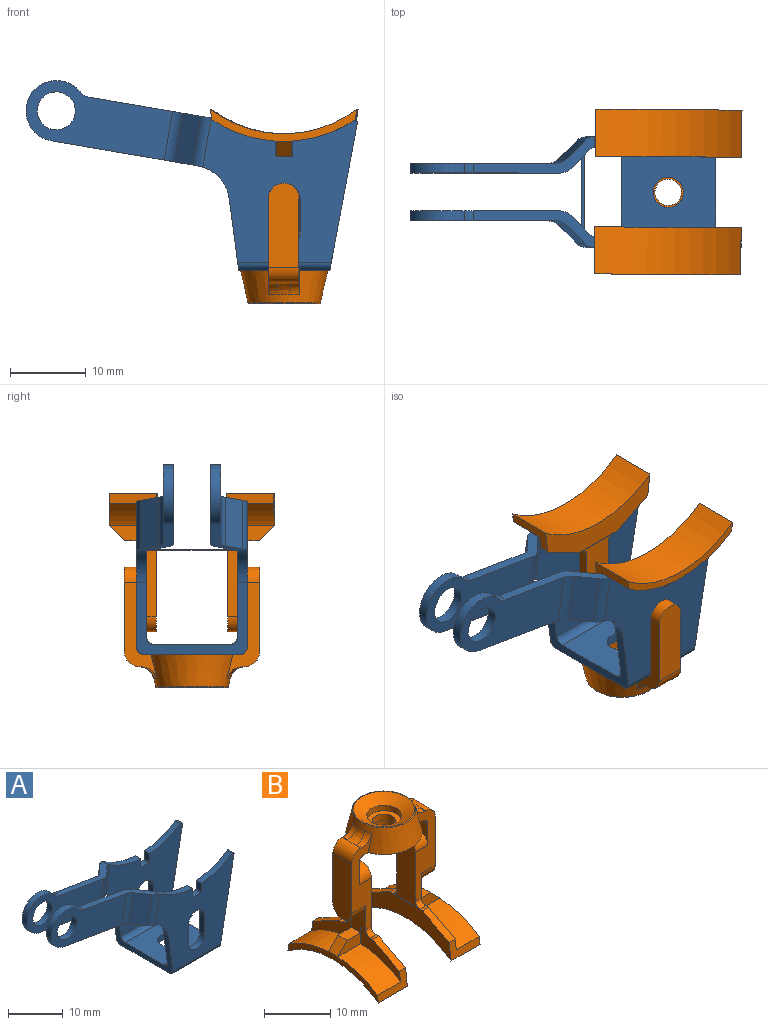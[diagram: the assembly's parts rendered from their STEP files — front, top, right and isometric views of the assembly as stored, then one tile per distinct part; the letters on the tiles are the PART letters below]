
ASSEMBLY  parts=2 mates=1
PART A: 66 faces, bbox 43.6x14.6x25 mm
  f0: plane 19.31x4.69mm, normal (-0.17,0,-0.99), area 27.2mm2, adj f4,f14,f45,f48,f49,f50,f54,f55
  f1: plane 19.31x4.69mm, normal (-0.17,0,-0.99), area 27.2mm2, adj f5,f14,f42,f43,f46,f47,f53,f57
  f2: cylinder r=2mm len=1.3mm, axis (0,1,0), area 1.9mm2, adj f4,f6,f45,f49
  f3: cylinder r=2mm len=1.3mm, axis (0,1,0), area 1.9mm2, adj f5,f7,f42,f46
  f4: cylinder r=4mm len=7.94mm, axis (0,1,0), area 20.1mm2, adj f0,f2,f45,f49
  f5: cylinder r=4mm len=7.94mm, axis (0,1,0), area 20.1mm2, adj f1,f3,f42,f46
  f6: plane 15.92x4.8mm, normal (0.17,0,0.99), area 22.9mm2, adj f2,f11,f45,f48,f49,f50,f54,f55
  f7: plane 15.92x4.8mm, normal (0.17,0,0.99), area 22.9mm2, adj f3,f10,f42,f43,f46,f47,f53,f57
  f8: plane 20.35x18.99mm, normal (0,-1,0), area 231.1mm2, adj f11,f14,f15,f17,f18,f19,f33,f34
  f9: plane 20.35x18.99mm, normal (0,1,0), area 231.1mm2, adj f10,f12,f13,f14,f15,f17,f24,f25
  f10: cylinder r=17mm len=8.63mm, axis (0,1,0), area 12.1mm2, adj f7,f9,f22,f31,f57,f59
  f11: cylinder r=17mm len=8.63mm, axis (0,1,0), area 12.1mm2, adj f6,f8,f21,f41,f56,f60
  f12: cylinder r=0.3mm len=1.3mm, axis (0,1,0), area 0.9mm2, adj f9,f13,f17,f22
  f13: cylinder r=17mm len=8.04mm, axis (0,1,0), area 11.1mm2, adj f9,f12,f22,f28
  f14: cylinder r=5mm len=14.6mm, axis (0,1,0), area 21mm2, adj f0,f1,f8,f9,f15,f21,f22,f23
  f15: plane 14.6x9.48mm, normal (-0.99,0,-0.13), area 40.6mm2, adj f8,f9,f14,f16,f20,f21,f22,f61
  f16: plane 12.6x12mm, normal (0,0,-1), area 138.6mm2, adj f15,f17,f63,f64,f65
  f17: plane 19.37x14.6mm, normal (0.98,0,-0.18), area 67.1mm2, adj f8,f9,f12,f16,f18,f20,f21,f22
  f18: cylinder r=0.3mm len=1.3mm, axis (0,1,0), area 0.9mm2, adj f8,f17,f19,f21
  f19: cylinder r=17mm len=8.04mm, axis (0,1,0), area 11.1mm2, adj f8,f18,f21,f40
  f20: plane 12.41x10mm, normal (0,0,1), area 111.6mm2, adj f15,f17,f61,f62,f65
  f21: plane 19.83x17.43mm, normal (0,1,0), area 211.3mm2, adj f11,f14,f15,f17,f18,f19,f33,f34
  f22: plane 19.83x17.43mm, normal (0,-1,0), area 211.3mm2, adj f10,f12,f13,f14,f15,f17,f24,f25
  f23: plane 11.64x0.01mm, normal (1,0,0), area 0.2mm2, adj f14,f44,f59,f60
  f24: plane 4.25x1.3mm, normal (1,0,0), area 5.5mm2, adj f9,f22,f25,f27
  f25: cylinder r=2.12mm len=4.25mm, axis (0,1,0), area 8.7mm2, adj f9,f22,f24,f26
  f26: plane 4.25x1.3mm, normal (-1,0,0), area 5.5mm2, adj f9,f22,f25,f27
  f27: cylinder r=2.12mm len=4.25mm, axis (0,1,0), area 8.7mm2, adj f9,f22,f24,f26
  f28: plane 1.84x1.3mm, normal (-1,0,0), area 2.4mm2, adj f9,f13,f22,f29
  f29: cylinder r=0.2mm len=1.3mm, axis (0,1,0), area 0.4mm2, adj f9,f22,f28,f32
  f30: cylinder r=0.2mm len=1.3mm, axis (0,1,0), area 0.4mm2, adj f9,f22,f31,f32
  f31: plane 1.84x1.3mm, normal (1,0,0), area 2.4mm2, adj f9,f10,f22,f30
  f32: plane 1.85x1.3mm, normal (0,0,1), area 2.4mm2, adj f9,f22,f29,f30
  f33: cylinder r=2.12mm len=4.25mm, axis (0,1,0), area 8.7mm2, adj f8,f21,f34,f36
  f34: plane 4.25x1.3mm, normal (-1,0,0), area 5.5mm2, adj f8,f21,f33,f35
  f35: cylinder r=2.12mm len=4.25mm, axis (0,1,0), area 8.7mm2, adj f8,f21,f34,f36
  f36: plane 4.25x1.3mm, normal (1,0,0), area 5.5mm2, adj f8,f21,f33,f35
  f37: plane 1.85x1.3mm, normal (0,0,1), area 2.4mm2, adj f8,f21,f38,f39
  f38: cylinder r=0.2mm len=1.3mm, axis (0,1,0), area 0.4mm2, adj f8,f21,f37,f40
  f39: cylinder r=0.2mm len=1.3mm, axis (0,1,0), area 0.4mm2, adj f8,f21,f37,f41
  f40: plane 1.84x1.3mm, normal (-1,0,0), area 2.4mm2, adj f8,f19,f21,f38
  f41: plane 1.84x1.3mm, normal (1,0,0), area 2.4mm2, adj f8,f11,f21,f39
  f42: plane 19.3x10.49mm, normal (0,1,0), area 106.9mm2, adj f1,f3,f5,f7,f52,f58
  f43: plane 6.8x3.39mm, normal (-0.7,0.71,0.12), area 21.4mm2, adj f1,f7,f57,f58
  f44: plane 11.64x0.36mm, normal (0.17,0,0.99), area 4.2mm2, adj f14,f23,f59,f60
  f45: plane 19.83x10.58mm, normal (0,1,0), area 110.4mm2, adj f0,f2,f4,f6,f51,f54
  f46: plane 19.83x10.58mm, normal (0,-1,0), area 110.4mm2, adj f1,f3,f5,f7,f52,f53
  f47: plane 6.8x3.39mm, normal (0.7,-0.71,-0.12), area 21.4mm2, adj f1,f7,f53,f59
  f48: plane 6.8x3.39mm, normal (0.7,0.71,-0.12), area 21.4mm2, adj f0,f6,f54,f60
  f49: plane 19.3x10.49mm, normal (0,-1,0), area 106.9mm2, adj f0,f2,f4,f6,f51,f55
  f50: plane 6.8x3.39mm, normal (-0.7,-0.71,0.12), area 21.4mm2, adj f0,f6,f55,f56
  f51: cylinder r=2.5mm len=5mm, axis (0,1,0), area 20.4mm2, adj f45,f49
  f52: cylinder r=2.5mm len=5mm, axis (0,1,0), area 20.4mm2, adj f42,f46
  f53: cylinder r=2mm len=6.65mm, axis (-0.17,0,-0.99), area 10.2mm2, adj f1,f7,f46,f47
  f54: cylinder r=2mm len=6.65mm, axis (-0.17,0,-0.99), area 10.2mm2, adj f0,f6,f45,f48
  f55: cylinder r=2mm len=6.65mm, axis (0.17,0,0.99), area 10.2mm2, adj f0,f6,f49,f50
  f56: cylinder r=2mm len=6.69mm, axis (-0.17,0,-0.99), area 10.2mm2, adj f0,f6,f8,f11,f14,f50
  f57: cylinder r=2mm len=6.69mm, axis (-0.17,0,-0.99), area 10.2mm2, adj f1,f7,f9,f10,f14,f43
  f58: cylinder r=2mm len=6.65mm, axis (0.17,0,0.99), area 10.2mm2, adj f1,f7,f42,f43
  f59: cylinder r=2mm len=6.79mm, axis (-0.17,0,-0.99), area 10.2mm2, adj f1,f7,f10,f14,f22,f23,f44,f47
  f60: cylinder r=2mm len=6.79mm, axis (-0.17,0,-0.99), area 10.2mm2, adj f0,f6,f11,f14,f21,f23,f44,f48
  f61: cylinder r=1mm len=12.73mm, axis (-1,0,0), area 19.7mm2, adj f15,f17,f20,f22
  f62: cylinder r=1mm len=12.73mm, axis (1,0,0), area 19.7mm2, adj f15,f17,f20,f21
  f63: cylinder r=1mm len=12.32mm, axis (1,0,0), area 19mm2, adj f9,f15,f16,f17
  f64: cylinder r=1mm len=12.32mm, axis (-1,0,0), area 19mm2, adj f8,f15,f16,f17
  f65: cylinder r=2mm len=4mm, axis (0,0,-1), area 16.3mm2, adj f16,f20
PART B: 79 faces, bbox 21.7x19.3x25.6 mm
  f0: plane 17.18x4.3mm, normal (0,-1,0), area 38.6mm2, adj f1,f15,f22,f23,f33,f34,f35,f36
  f1: plane 5.5x4mm, normal (-1,0,0), area 13.7mm2, adj f0,f2,f32,f42,f65,f66,f69,f72
  f2: plane 2.85x2mm, normal (0,0,1), area 5.7mm2, adj f1,f65,f72,f74
  f3: plane 7x1.3mm, normal (0,0,1), area 1.6mm2, adj f35,f52,f55,f56,f68,f70,f77,f78
  f4: plane 6.2x3.22mm, normal (0,-0.99,0.12), area 10.9mm2, adj f5,f52,f53,f56,f67,f68
  f5: plane 19.26x4.22mm, normal (-1,0,0), area 20.4mm2, adj f4,f53,f54,f65,f67,f71,f72,f74
  f6: plane 17.18x4.3mm, normal (0,1,0), area 38.6mm2, adj f7,f14,f22,f23,f26,f27,f28,f30
  f7: plane 5.5x4mm, normal (1,0,0), area 13.7mm2, adj f6,f9,f25,f39,f57,f60,f62,f63
  f8: plane 7x1.3mm, normal (0,0,1), area 1.6mm2, adj f10,f12,f26,f51,f58,f64,f75,f76
  f9: plane 2.85x2mm, normal (0,0,1), area 5.7mm2, adj f7,f60,f62,f73
  f10: plane 5.73x3mm, normal (0,-0.46,0.89), area 8.4mm2, adj f8,f49,f51,f64
  f11: plane 6.2x3.22mm, normal (0,0.99,0.12), area 10.9mm2, adj f12,f13,f50,f51,f58,f59
  f12: plane 5.73x3mm, normal (0,0.46,0.89), area 8.4mm2, adj f8,f11,f51,f58
  f13: plane 19.26x4.22mm, normal (1,0,0), area 20.4mm2, adj f11,f49,f50,f59,f60,f61,f62,f73
  f14: plane 0.93x0.21mm, normal (0,0,1), area 0.1mm2, adj f6,f28,f46
  f15: plane 0.93x0.21mm, normal (0,0,1), area 0.1mm2, adj f0,f33,f45
  f16: plane 4x4mm, normal (0,0,-1), area 2.9mm2, adj f17,f24
  f17: cylinder r=1.75mm len=3.5mm, axis (0,0,-1), area 12.9mm2, adj f16,f18
  f18: plane 5.25x5.25mm, normal (0,0,1), area 12mm2, adj f17,f19
  f19: cylinder r=2.62mm len=5.25mm, axis (0,0,-1), area 16.5mm2, adj f18,f20
  f20: cone r=4.63mm half-angle=60deg, axis (0,0,1), area 52.9mm2, adj f19,f21
  f21: torus R=4.68mm, axis (0,0,-1), area 5.5mm2, adj f20,f22
  f22: cone r=4.78mm half-angle=12.8deg, axis (0,0,-1), area 118.2mm2, adj f0,f6,f21,f23,f25,f32,f43,f44
  f23: plane 12.6x11.5mm, normal (0,0,-1), area 96.6mm2, adj f0,f6,f22,f24,f25,f30,f32,f37
  f24: cylinder r=2mm len=4mm, axis (0,0,-1), area 12.6mm2, adj f16,f23
  f25: plane 17.18x4.3mm, normal (0,-1,0), area 38.6mm2, adj f7,f22,f23,f26,f27,f28,f29,f30
  f26: plane 12x6mm, normal (-1,0,0), area 46.7mm2, adj f6,f8,f25,f40,f75,f76
  f27: plane 11.1x4mm, normal (1,0,0), area 42.7mm2, adj f6,f25,f28,f39
  f28: cylinder r=2mm len=4mm, axis (0,1,0), area 12.5mm2, adj f6,f14,f25,f27,f29,f47
  f29: plane 0.93x0.21mm, normal (0,0,1), area 0.1mm2, adj f25,f28,f48
  f30: cylinder r=1mm len=4mm, axis (0,1,0), area 6.3mm2, adj f6,f23,f25,f31
  f31: plane 4x4mm, normal (-1,0,0), area 9.7mm2, adj f6,f25,f30,f40
  f32: plane 17.18x4.3mm, normal (0,1,0), area 38.6mm2, adj f1,f22,f23,f33,f34,f35,f36,f37
  f33: cylinder r=2mm len=4mm, axis (0,1,0), area 12.5mm2, adj f0,f15,f32,f34,f38,f44
  f34: plane 11.1x4mm, normal (-1,0,0), area 42.7mm2, adj f0,f32,f33,f42
  f35: plane 12x6mm, normal (1,0,0), area 46.7mm2, adj f0,f3,f32,f41,f77,f78
  f36: plane 4x4mm, normal (1,0,0), area 9.7mm2, adj f0,f32,f37,f41
  f37: cylinder r=1mm len=4mm, axis (0,1,0), area 6.3mm2, adj f0,f23,f32,f36
  f38: plane 0.93x0.21mm, normal (0,0,1), area 0.1mm2, adj f32,f33,f43
  f39: cylinder r=2mm len=4mm, axis (-1,0,0), area 18.2mm2, adj f6,f7,f25,f27
  f40: cylinder r=2mm len=4mm, axis (1,0,0), area 16.3mm2, adj f6,f25,f26,f31
  f41: cylinder r=2mm len=4mm, axis (1,0,0), area 16.3mm2, adj f0,f32,f35,f36
  f42: cylinder r=2mm len=4mm, axis (-1,0,0), area 18.2mm2, adj f0,f1,f32,f34
  f43: torus R=6.98mm, axis (0,0,-1), area 3.1mm2, adj f22,f32,f38,f44
  f44: bspline ~4.76x2.2mm, area 4.8mm2, adj f22,f33,f43,f45
  f45: torus R=6.98mm, axis (0,0,-1), area 3.1mm2, adj f0,f15,f22,f44
  f46: torus R=6.98mm, axis (0,0,1), area 3.1mm2, adj f6,f14,f22,f47
  f47: bspline ~4.76x2.2mm, area 4.8mm2, adj f22,f28,f46,f48
  f48: torus R=6.98mm, axis (0,0,1), area 3.1mm2, adj f22,f25,f29,f47
  f49: plane 6.2x3.22mm, normal (0,-0.99,0.12), area 10.9mm2, adj f10,f13,f50,f51,f61,f64
  f50: cylinder r=16mm len=19.26mm, axis (-1,0,0), area 128.1mm2, adj f11,f13,f49,f51
  f51: plane 19.26x6.22mm, normal (-1,0,0), area 56.7mm2, adj f8,f10,f11,f12,f49,f50
  f52: plane 5.73x3mm, normal (0,-0.46,0.89), area 8.4mm2, adj f3,f4,f56,f68
  f53: cylinder r=16mm len=19.26mm, axis (1,0,0), area 128.1mm2, adj f4,f5,f54,f56
  f54: plane 6.2x3.22mm, normal (0,0.99,0.12), area 10.9mm2, adj f5,f53,f55,f56,f70,f71
  f55: plane 5.73x3mm, normal (0,0.46,0.89), area 8.4mm2, adj f3,f54,f56,f70
  f56: plane 19.26x6.22mm, normal (1,0,0), area 56.7mm2, adj f3,f4,f52,f53,f54,f55
  f57: plane 1x0.05mm, normal (0,0,-1), area 0mm2, adj f6,f7,f58,f60
  f58: plane 8.46x5.88mm, normal (1,0,0), area 17.4mm2, adj f8,f11,f12,f57,f59,f60,f75
  f59: cylinder r=17mm len=8.46mm, axis (-1,0,0), area 44.3mm2, adj f11,f13,f58,f60
  f60: plane 4.9x3.03mm, normal (0,1,0), area 8mm2, adj f7,f9,f13,f57,f58,f59,f73
  f61: cylinder r=17mm len=8.46mm, axis (-1,0,0), area 44.3mm2, adj f13,f49,f62,f64
  f62: plane 4.9x3.03mm, normal (0,-1,0), area 8mm2, adj f7,f9,f13,f61,f63,f64,f73
  f63: plane 1x0.05mm, normal (0,0,-1), area 0mm2, adj f7,f25,f62,f64
  f64: plane 8.46x5.88mm, normal (1,0,0), area 17.4mm2, adj f8,f10,f49,f61,f62,f63,f76
  f65: plane 4.9x3.03mm, normal (0,-1,0), area 8mm2, adj f1,f2,f5,f66,f67,f68,f74
  f66: plane 1x0.05mm, normal (0,0,-1), area 0mm2, adj f0,f1,f65,f68
  f67: cylinder r=17mm len=8.46mm, axis (1,0,0), area 44.3mm2, adj f4,f5,f65,f68
  f68: plane 8.46x5.88mm, normal (-1,0,0), area 17.4mm2, adj f3,f4,f52,f65,f66,f67,f78
  f69: plane 1x0.05mm, normal (0,0,-1), area 0mm2, adj f1,f32,f70,f72
  f70: plane 8.46x5.88mm, normal (-1,0,0), area 17.4mm2, adj f3,f54,f55,f69,f71,f72,f77
  f71: cylinder r=17mm len=8.46mm, axis (1,0,0), area 44.3mm2, adj f5,f54,f70,f72
  f72: plane 4.9x3.03mm, normal (0,1,0), area 8mm2, adj f1,f2,f5,f69,f70,f71,f74
  f73: plane 2x2mm, normal (0.71,0,0.71), area 5.7mm2, adj f9,f13,f60,f62
  f74: plane 2x2mm, normal (-0.71,0,0.71), area 5.7mm2, adj f2,f5,f65,f72
  f75: cylinder r=1mm len=1.25mm, axis (-1,0,0), area 2mm2, adj f6,f8,f26,f58
  f76: cylinder r=1mm len=1.25mm, axis (1,0,0), area 2mm2, adj f8,f25,f26,f64
  f77: cylinder r=1mm len=1.25mm, axis (-1,0,0), area 2mm2, adj f3,f32,f35,f70
  f78: cylinder r=1mm len=1.25mm, axis (1,0,0), area 2mm2, adj f0,f3,f35,f68
PLACE A at identity fixed
PLACE B rot(axis=(0.71,0.7,0),180deg) t=(0,0,-0.02)mm
MATE cylindrical B.f17 <-> A.f65  axis (0,0,1) through (0,0,-3.19)mm
